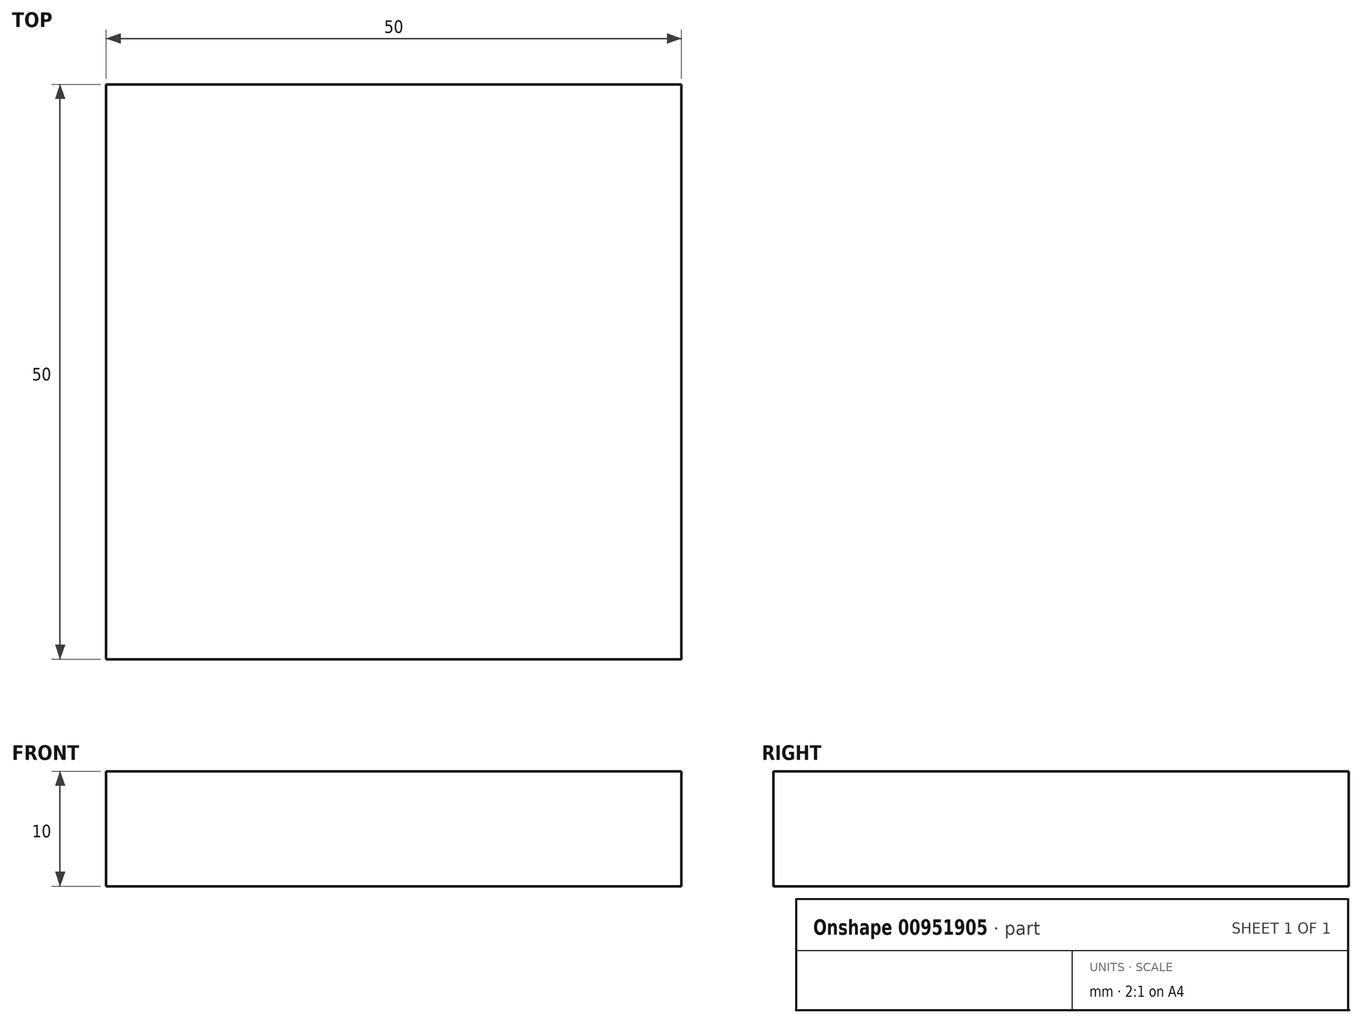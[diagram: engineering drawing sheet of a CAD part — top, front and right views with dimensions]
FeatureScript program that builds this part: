
annotation { "Feature Type Name" : "Feature", "Feature Type Description" : "" }
export const myFeature = defineFeature(function(context is Context, id is Id, definition is map)
    precondition{}
    {
        {
            var Q0;
            Q0=qCreatedBy(makeId("Top.planeOp"),FACE);
            var sketch = newSketch(context, id + "F0", { "sketchPlane" : qUnion([Q0])});
            skLineSegment(sketch, "E0.bottom", {"start": v(25, 25) * mm, "end": v(-25, 25) * mm});
            skLineSegment(sketch, "E0.top", {"start": v(25, -25) * mm, "end": v(-25, -25) * mm});
            skLineSegment(sketch, "E0.left", {"start": v(25, 25) * mm, "end": v(25, -25) * mm});
            skLineSegment(sketch, "E0.right", {"start": v(-25, 25) * mm, "end": v(-25, -25) * mm});
            skPoint(sketch, "E0.middle", {"position": v(0, 0) * mm});
            skSolve(sketch);
        }
        {
            var Q0;
            Q0=makeQuery(id+"F0.imprint","IMPRINT",FACE,{"disambiguationData":[TD([[makeQuery(id+"F0.imprint","IMPRINT",EDGE,{"derivedFrom":sQuery(id+"F0.wireOp",EDGE,"E0.bottom")}),1.0]])]});
            extrude(context, id + "F1", {"entities" : qUnion([Q0]), "depth" : 10 * mm, "offsetDistance" : 25.4 * mm});
        }
    });
